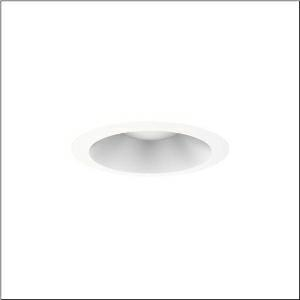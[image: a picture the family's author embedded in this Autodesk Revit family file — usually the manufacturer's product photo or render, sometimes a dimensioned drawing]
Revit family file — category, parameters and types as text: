
# Revit family: lunis_31-xl_51dn16mg32b
name_source: partatom
category: Lighting Fixtures
units: mm (PartAtom-declared; Revit-internal decimal feet)

## family parameters
Cut with Voids When Loaded = No
Host = Face
Light Source = No
Part Type = Normal
Room Calculation Point = No
Round Connector Dimension = Use Diameter
Shared = No

## types (1)
- --- (1 x LED, 2500 lm, 17 W, 3000K)
    Apparent Load = 17 VA
    CIE Flux Codes = 64 93 99 100 100
    Color Rendering = 80
    Color Temperature = 3000K
    Default Elevation = 1800 mm
    Description = Lunis 31, -XL, downlight, light control with reflector, light emission: direct distribution, LED rated luminous flux: 2.500lm, light colour: 830, mains connection: 220..240V, AC, 50/60Hz, housing, of aluminium, white, protection rating (complete): IP20, protection rating (on room side): IP54, insulation class (complete): insulation class II (safety insulation), certification: CE, packaging unit: 1 piece
    Height = 0 mm  [stored 0 ft]
    Lamp = 1 x LED
    Lamp Light Flux = 2500 lm
    Lamp Power = 17 W
    Lamp count = 1
    Length = 259 mm
    Luminous efficacy = 147 lm/W
    Manufacturer = Siteco
    ModVariant = No
    Model = 51DN16MG32B
    Mounting Place = Ceiling
    Mounting Type = Recessed
    Number of Poles = 1
    OnlyDefault = Yes
    Power Factor = 1
    Product Name = Lunis 31-XL
    Product group = downlight
    ProductGroupID = 400
    Protection Class = Protection class II
    Protection Degree = IP 20
    RLX_Detail_Level = 1
    RLX_Emergency_Light_Flux = 0 lm
    RLX_Emergency_Type = 0
    RLX_Emergency_Type_DB = No
    RlxData = <blob elided: 24369 chars, md5=dd14c368>
    Socket = socket
    Standby Power = 0 W
    System Light Flux = 2500 lm
    System Power = 17 W
    Type Comments = individual setting: luminous flux: 100 % | (ON | ON | ON | OFF) | 450 mA
    Type Image = l_1345915.jpg
    URL = http://relux.com
    VarID = @adj_010117
    Voltage = 0 V
    Weight = 0.00 kg
    Width = 0 mm  [stored 0 ft]

note: [stored X ft] marks values corroborated as IEEE doubles in the binary element streams (Revit-internal decimal feet)

## geometry (parser evidence)
native form markers: Blend x4, Sweep x12
no freeform markers — native parametric forms only
